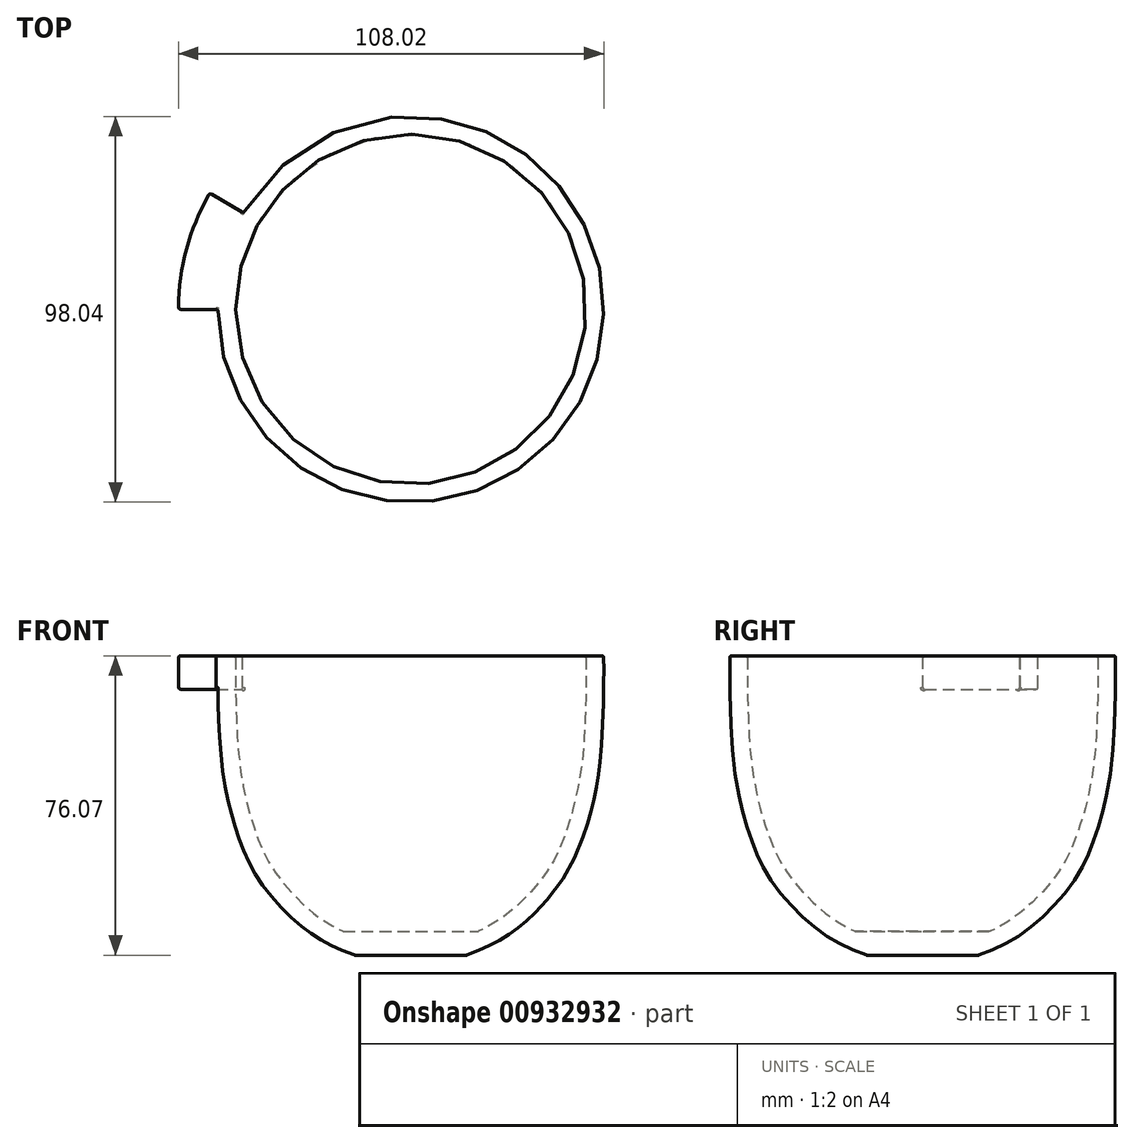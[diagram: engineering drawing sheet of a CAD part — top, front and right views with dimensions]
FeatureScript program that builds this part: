
annotation { "Feature Type Name" : "Feature", "Feature Type Description" : "" }
export const myFeature = defineFeature(function(context is Context, id is Id, definition is map)
    precondition{}
    {
        {
            var Q0;
            Q0=qCreatedBy(makeId("Front.planeOp"),FACE);
            var sketch = newSketch(context, id + "F0", { "sketchPlane" : qUnion([Q0])});
            skLineSegment(sketch, "E0", {"start": v(0, 78.82) * mm, "end": v(-49, 78.82) * mm});
            skLineSegment(sketch, "E1", {"start": v(0, 0) * mm, "end": v(0, 78.82) * mm});
            skFitSpline(sketch, "E2", {"points": [v(-49, 78.82) * mm, v(-49, 71.2) * mm, v(-47.95, 50.94) * mm, v(-44.24, 34.32) * mm, v(-38.54, 21.8) * mm, v(-27.37, 9.77) * mm, v(-17.3, 3.96) * mm, v(0, 0) * mm], "startDerivative": vector(-0.53, -120.05) * mm, "endDerivative": vector(126.32, 0) * mm});
            skSolve(sketch);
        }
        {
            var Q0;
            Q0=qSketchRegion(id+"F0",true);
            var Q1;
            Q1=sQuery(id+"F0.wireOp",EDGE,"E1");
            revolve(context, id + "F1", {"surfaceOperationType" : NewSurfaceOperationType.NEW, "entities" : qUnion([Q0]), "axis" : qUnion([Q1]), "revolveType" : RevolveType.FULL});
        }
        {
            var Q0;
            Q0=makeQuery(id+"F1.opRevolve","SWEPT_FACE",FACE,{"disambiguationData":[OSD([sQuery(id+"F0.wireOp",EDGE,"E0")])]});
            shell(context, id + "F2", {"entities" : qUnion([Q0]), "thickness" : 4.5 * mm});
        }
        {
            var Q0;
            Q0=qCreatedBy(makeId("Front.planeOp"),FACE);
            var sketch = newSketch(context, id + "F3", { "sketchPlane" : qUnion([Q0])});
            skLineSegment(sketch, "E3", {"start": v(-41.77, 30.38) * mm, "end": v(-53.43, 30.38) * mm});
            skLineSegment(sketch, "E4", {"start": v(-49.23, 20.12) * mm, "end": v(-36.53, 20.12) * mm});
            skLineSegment(sketch, "E5", {"start": v(-36.53, 20.12) * mm, "end": v(-41.77, 30.38) * mm});
            skFitSpline(sketch, "E6", {"points": [v(-42.03, 8) * mm, v(-47.44, 16.94) * mm, v(-49.23, 20.12) * mm, v(-51.33, 24.44) * mm, v(-53.43, 30.38) * mm, v(-55.23, 38.72) * mm, v(-56.67, 49.18) * mm, v(-57.32, 61.86) * mm, v(-57.58, 68.13) * mm, v(-57.6, 68.09) * mm], "startDerivative": vector(-47.1, 69.03) * mm, "endDerivative": vector(-6.03, -13.35) * mm});
            skLineSegment(sketch, "E7", {"start": v(-57.58, 68.13) * mm, "end": v(-69.83, 68.13) * mm});
            skFitSpline(sketch, "E8", {"points": [v(-69.83, 68.13) * mm, v(-69.83, 61.07) * mm, v(-69.06, 51.29) * mm, v(-67.63, 40.46) * mm, v(-65.54, 31.18) * mm, v(-63.64, 25) * mm, v(-58.64, 14.66) * mm, v(-54.3, 8) * mm], "startDerivative": vector(-1.12, -53.42) * mm, "endDerivative": vector(31.44, -44.67) * mm});
            skLineSegment(sketch, "E9", {"start": v(-54.3, 8) * mm, "end": v(-42.03, 8) * mm});
            skSolve(sketch);
        }
        {
            var Q0;
            Q0=qCreatedBy(makeId("Right.planeOp"),FACE);
            cPlane(context, id + "F4", {"entities" : qUnion([Q0]), "cplaneType" : CPlaneType.OFFSET, "offset" : 65 * mm, "oppositeDirection" : true, "width" : 150 * mm, "height" : 150 * mm});
        }
        {
            var Q0;
            Q0=qCreatedBy(id+"F4.planeOp",FACE);
            var sketch = newSketch(context, id + "F5", { "sketchPlane" : qUnion([Q0])});
            skPoint(sketch, "E10.middle", {"position": v(0, 24.44) * mm});
            skCircle(sketch, "E11", {"center": v(10, 68.82) * mm, "radius": 6 * mm});
            skSolve(sketch);
        }
        {
            var Q0;
            Q0=qCreatedBy(makeId("Top.planeOp"),FACE);
            cPlane(context, id + "F6", {"entities" : qUnion([Q0]), "cplaneType" : CPlaneType.OFFSET, "offset" : 8 * mm, "width" : 150 * mm, "height" : 150 * mm});
        }
        {
            var Q0;
            Q0=qCreatedBy(makeId("Front.planeOp"),FACE);
            var sketch = newSketch(context, id + "F7", { "sketchPlane" : qUnion([Q0])});
            skLineSegment(sketch, "E12", {"start": v(0, 1.35) * mm, "end": v(0, 8.85) * mm});
            skLineSegment(sketch, "E13", {"start": v(0, 8.85) * mm, "end": v(-21, 8.85) * mm});
            skLineSegment(sketch, "E14", {"start": v(-21, 8.85) * mm, "end": v(0, 1.35) * mm});
            skSolve(sketch);
        }
        {
            var Q0;
            Q0=qSketchRegion(id+"F7",true);
            var Q1;
            Q1=sQuery(id+"F7.wireOp",EDGE,"E12");
            revolve(context, id + "F8", {"operationType" : NewBodyOperationType.ADD, "surfaceOperationType" : NewSurfaceOperationType.NEW, "entities" : qUnion([Q0]), "axis" : qUnion([Q1]), "revolveType" : RevolveType.FULL});
        }
        {
            var Q0;
            Q0=qCreatedBy(makeId("Front.planeOp"),FACE);
            var sketch = newSketch(context, id + "F9", { "sketchPlane" : qUnion([Q0])});
            skLineSegment(sketch, "E15.bottom", {"start": v(20, 0) * mm, "end": v(-20, 0) * mm});
            skLineSegment(sketch, "E15.top", {"start": v(20, 2.75) * mm, "end": v(-20, 2.75) * mm});
            skLineSegment(sketch, "E15.left", {"start": v(20, 0) * mm, "end": v(20, 2.75) * mm});
            skLineSegment(sketch, "E15.right", {"start": v(-20, 0) * mm, "end": v(-20, 2.75) * mm});
            skSolve(sketch);
        }
        {
            var Q0;
            Q0=qSketchRegion(id+"F9",true);
            extrude(context, id + "F10", {"entities" : qUnion([Q0]), "operationType" : NewBodyOperationType.REMOVE, "oppositeDirection" : true, "depth" : 40 * mm, "offsetDistance" : 25 * mm, "symmetric" : true});
        }
        {
            var Q0;
            Q0=qCreatedBy(makeId("Front.planeOp"),FACE);
            var sketch = newSketch(context, id + "F11", { "sketchPlane" : qUnion([Q0])});
            skLineSegment(sketch, "E16", {"start": v(-48, 78.82) * mm, "end": v(-59, 78.82) * mm});
            skLineSegment(sketch, "E17", {"start": v(-59, 78.82) * mm, "end": v(-59, 70.32) * mm});
            skLineSegment(sketch, "E18", {"start": v(-59, 70.32) * mm, "end": v(-48, 70.32) * mm});
            skLineSegment(sketch, "E19", {"start": v(-48, 70.32) * mm, "end": v(-48, 78.82) * mm});
            skSolve(sketch);
        }
        {
            var Q0;
            Q0=makeQuery(id+"F11.imprint","IMPRINT",FACE,{"disambiguationData":[TD([[makeQuery(id+"F11.imprint","IMPRINT",EDGE,{"derivedFrom":sQuery(id+"F11.wireOp",EDGE,"E16")}),1.0]])]});
            var Q1;
            Q1=sQuery(id+"F0.wireOp",EDGE,"E1");
            revolve(context, id + "F12", {"operationType" : NewBodyOperationType.ADD, "surfaceOperationType" : NewSurfaceOperationType.NEW, "entities" : qUnion([Q0]), "axis" : qUnion([Q1]), "revolveType" : RevolveType.ONE_DIRECTION, "oppositeDirection" : true, "angle" : 30 * degree});
        }
        {
            var Q0;
            Q0=makeQuery(id+"F10.boolean.opBoolean","INTERSECT",EDGE,{"derivedFrom":[makeQuery(id+"F1.opRevolve","SWEPT_FACE",FACE,{"disambiguationData":[OSD([sQuery(id+"F0.wireOp",EDGE,"E2")])]}),makeQuery(id+"F10.opExtrude","SWEPT_FACE",FACE,{"disambiguationData":[OSD([sQuery(id+"F9.wireOp",EDGE,"E15.top")])]})]});
            var Q1;
            Q1=makeQuery(id+"F8.boolean.opBoolean","INTERSECT",EDGE,{"derivedFrom":[makeQuery(id+"F2.opShell","OFFSET_FACE",FACE,{"disambiguationData":[OSD([sQuery(id+"F0.wireOp",EDGE,"E2")])]}),makeQuery(id+"F8.opRevolve","SWEPT_FACE",FACE,{"disambiguationData":[OSD([sQuery(id+"F7.wireOp",EDGE,"E13")])]})]});
            var Q2;
            Q2=makeQuery(id+"F12.boolean.opBoolean","MERGE",FACE,{"derivedFrom":[makeQuery(id+"F1.opRevolve","SWEPT_FACE",FACE,{"disambiguationData":[OSD([sQuery(id+"F0.wireOp",EDGE,"E0")])]}),makeQuery(id+"F12.opRevolve","SWEPT_FACE",FACE,{"disambiguationData":[OSD([sQuery(id+"F11.wireOp",EDGE,"E16")])]})]});
            var Q3;
            Q3=makeQuery(id+"F12.opRevolve","SWEPT_FACE",FACE,{"disambiguationData":[OSD([sQuery(id+"F11.wireOp",EDGE,"E17")])]});
            var Q4;
            Q4=makeQuery(id+"F12.opRevolve","CAP_FACE",FACE,{"disambiguationData":[OSD([sQuery(id+"F11.wireOp",EDGE,"E16"),sQuery(id+"F11.wireOp",EDGE,"E17"),sQuery(id+"F11.wireOp",EDGE,"E18"),sQuery(id+"F11.wireOp",EDGE,"E19")])],"isStart":true});
            var Q5;
            Q5=makeQuery(id+"F12.opRevolve","CAP_FACE",FACE,{"disambiguationData":[OSD([sQuery(id+"F11.wireOp",EDGE,"E16"),sQuery(id+"F11.wireOp",EDGE,"E17"),sQuery(id+"F11.wireOp",EDGE,"E18"),sQuery(id+"F11.wireOp",EDGE,"E19")])],"isStart":false});
            var Q6;
            Q6=makeQuery(id+"F12.opRevolve","SWEPT_FACE",FACE,{"disambiguationData":[OSD([sQuery(id+"F11.wireOp",EDGE,"E18")])]});
            fillet(context, id + "F13", {"entities" : qUnion([Q0, Q1, Q2, Q3, Q4, Q5, Q6]), "tangentPropagation" : true, "radius" : .5 * mm, "defaultsChanged" : false, "vertexSettings" : [], "allowEdgeOverflow" : false});
        }
    });
